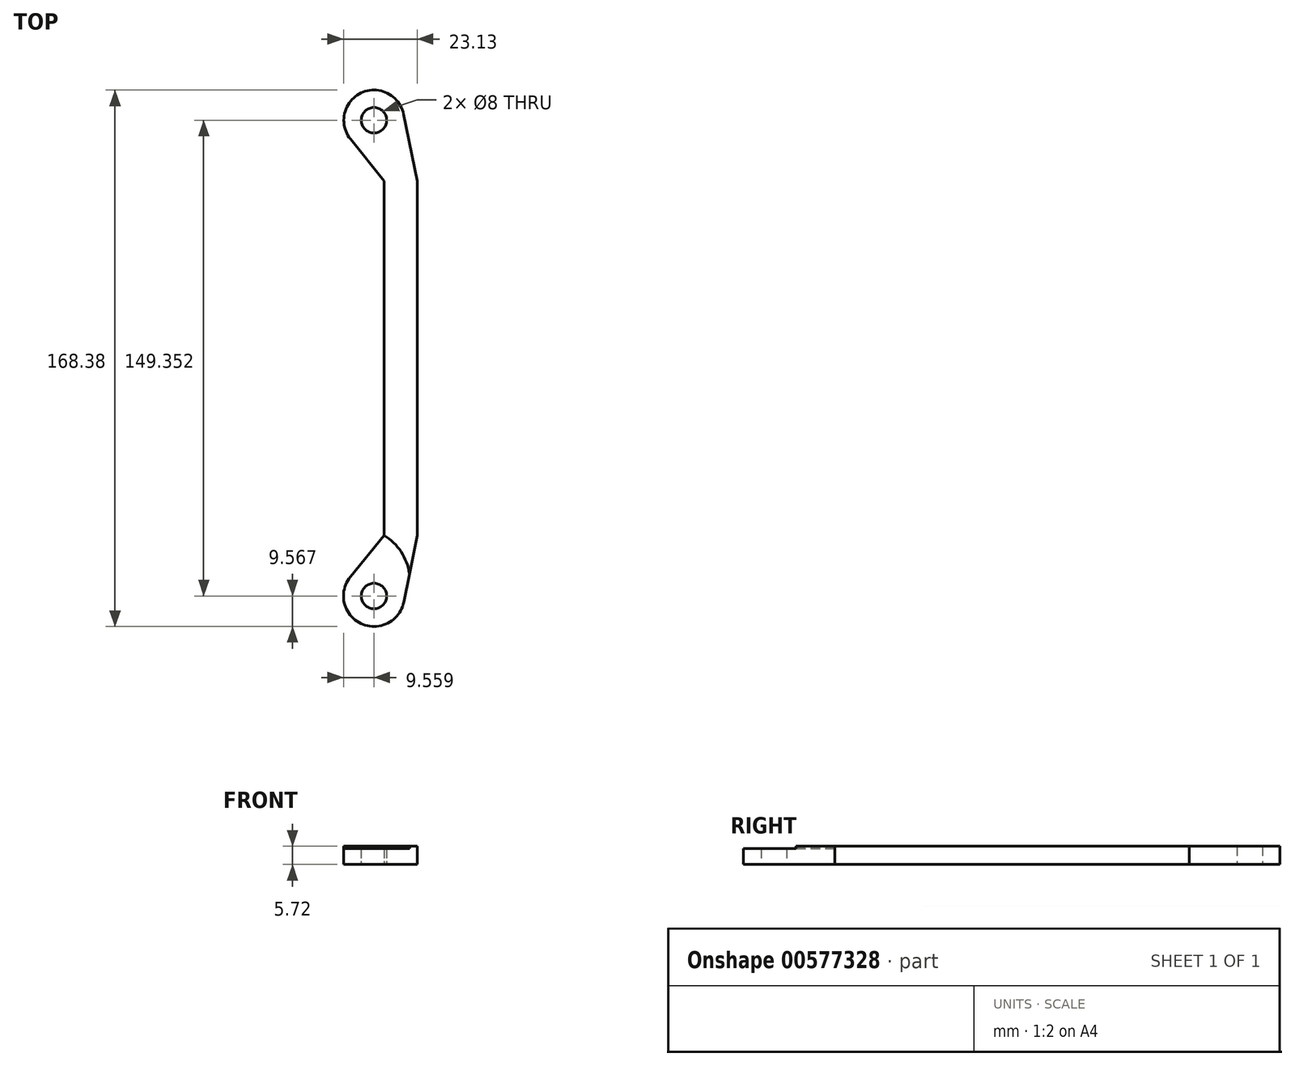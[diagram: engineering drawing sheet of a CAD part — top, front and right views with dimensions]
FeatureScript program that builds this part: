
annotation { "Feature Type Name" : "Feature", "Feature Type Description" : "" }
export const myFeature = defineFeature(function(context is Context, id is Id, definition is map)
    precondition{}
    {
        {
            var Q0;
            Q0=qCreatedBy(makeId("Top.planeOp"),FACE);
            var sketch = newSketch(context, id + "F0", { "sketchPlane" : qUnion([Q0])});
            skCircle(sketch, "E0", {"center": v(-2.02, 74.68) * mm, "radius": 4 * mm});
            skCircle(sketch, "E1", {"center": v(-2.02, -74.67) * mm, "radius": 4 * mm});
            skCircle(sketch, "E2", {"center": v(-2.02, 74.68) * mm, "radius": 9.46 * mm});
            skCircle(sketch, "E3", {"center": v(-2.02, -74.67) * mm, "radius": 9.56 * mm});
            skLineSegment(sketch, "E4", {"start": v(1.18, 55.62) * mm, "end": v(-9.39, 68.74) * mm});
            skLineSegment(sketch, "E5", {"start": v(11.55, 55.62) * mm, "end": v(7.25, 76.58) * mm});
            skLineSegment(sketch, "E6", {"start": v(1.18, 55.62) * mm, "end": v(1.18, -55.61) * mm});
            skLineSegment(sketch, "E7", {"start": v(1.18, -55.61) * mm, "end": v(-9.43, -68.63) * mm});
            skLineSegment(sketch, "E8", {"start": v(11.55, -55.61) * mm, "end": v(11.55, 55.62) * mm});
            skLineSegment(sketch, "E9", {"start": v(11.55, -55.61) * mm, "end": v(7.36, -76.55) * mm});
            skSolve(sketch);
        }
        {
            var Q0;
            Q0 = qSketchRegion(id + "F0", true);
            extrude(context, id + "F1", {"entities" : qUnion([Q0]), "endBound" : BoundingType.SYMMETRIC, "depth" : 5.7 * mm, "offsetDistance" : 25.4 * mm});
        }
        {
            var Q0;
            Q0=makeQuery(id+"F1.opExtrude","CAP_FACE",FACE,{"disambiguationData":[OSD([sQuery(id+"F0.wireOp",EDGE,"E0"),sQuery(id+"F0.wireOp",EDGE,"E1"),sQuery(id+"F0.wireOp",EDGE,"E2"),sQuery(id+"F0.wireOp",EDGE,"E3"),sQuery(id+"F0.wireOp",EDGE,"E4"),sQuery(id+"F0.wireOp",EDGE,"E5"),sQuery(id+"F0.wireOp",EDGE,"E6"),sQuery(id+"F0.wireOp",EDGE,"E7"),sQuery(id+"F0.wireOp",EDGE,"E8"),sQuery(id+"F0.wireOp",EDGE,"E9")])],"isStart":false});
            var sketch = newSketch(context, id + "F2", { "sketchPlane" : qUnion([Q0])});
            skArc(sketch, "E10", {"start": v(9.12, -67.73) * mm, "mid": v(6.5, -60.79) * mm, "end": v(1.18, -55.61) * mm});
            skSolve(sketch);
        }
        {
            var Q0;
            {var subQ1=sQuery(id+"F2.wireOp",EDGE,"E10");Q0=makeQuery(id+"F2.imprint","IMPRINT",FACE,{"disambiguationData":[TD([[makeQuery(id+"F2.imprint","IMPRINT",EDGE,{"derivedFrom":subQ1}),1.0]])]});}
            extrude(context, id + "F3", {"entities" : qUnion([Q0]), "operationType" : NewBodyOperationType.REMOVE, "oppositeDirection" : true, "depth" : 0.76 * mm, "offsetDistance" : 25.4 * mm});
        }
    });
